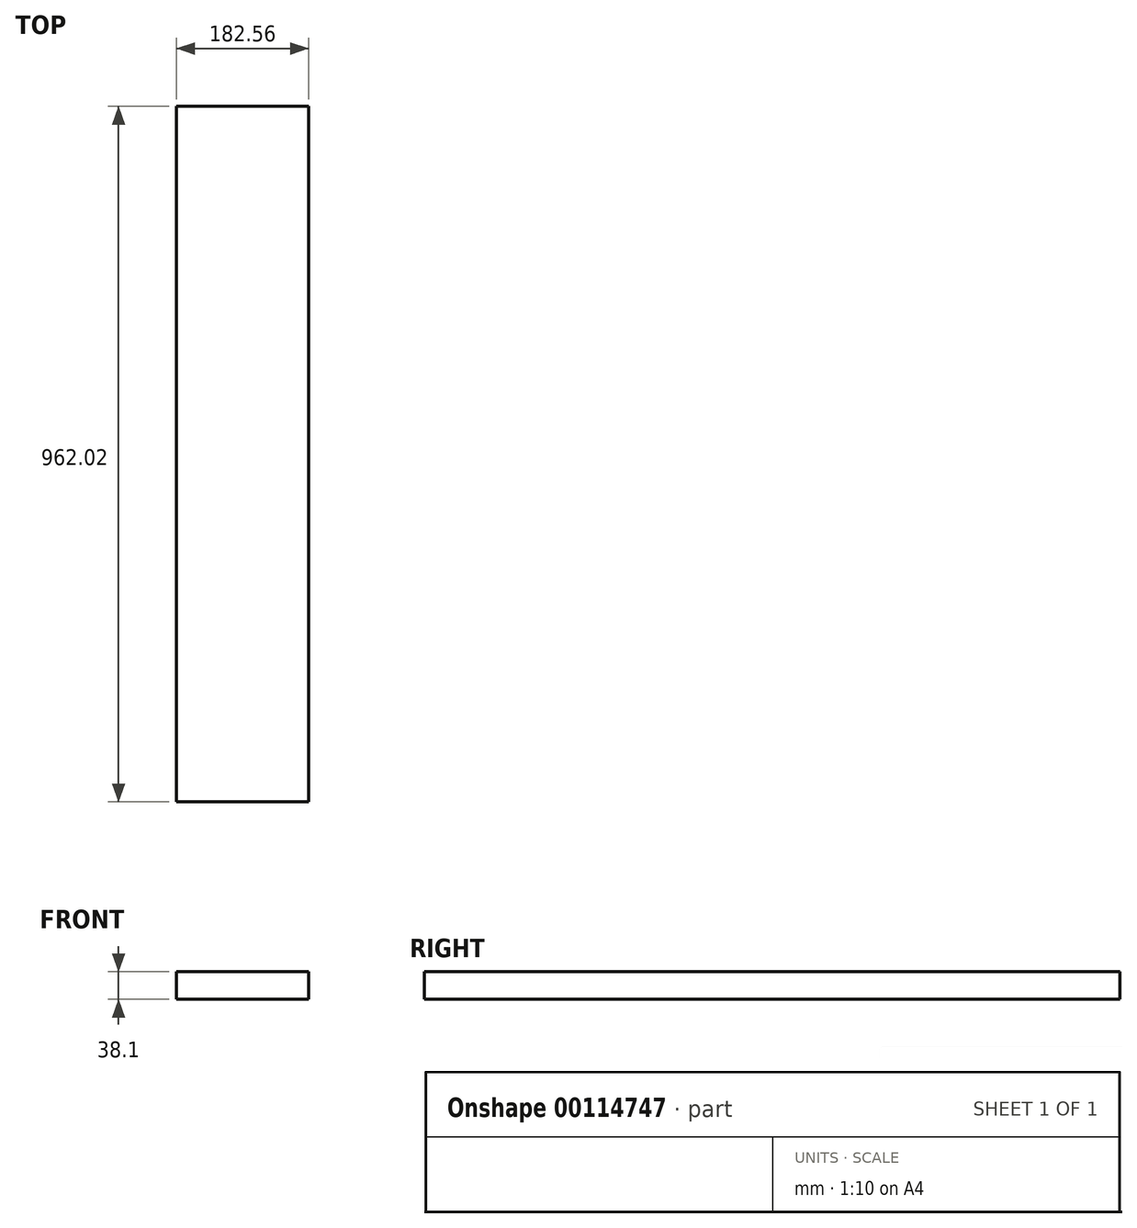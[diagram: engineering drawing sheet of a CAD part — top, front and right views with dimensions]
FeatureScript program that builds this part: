
annotation { "Feature Type Name" : "Feature", "Feature Type Description" : "" }
export const myFeature = defineFeature(function(context is Context, id is Id, definition is map)
    precondition{}
    {
        {
            var Q0;
            Q0=qCreatedBy(makeId("Top.planeOp"),FACE);
            var sketch = newSketch(context, id + "F0", { "sketchPlane" : qUnion([Q0])});
            skLineSegment(sketch, "E0.bottom", {"start": v(0, 0) * mm, "end": v(182.56, 0) * mm});
            skLineSegment(sketch, "E0.top", {"start": v(0, 962.03) * mm, "end": v(182.56, 962.03) * mm});
            skLineSegment(sketch, "E0.left", {"start": v(0, 0) * mm, "end": v(0, 962.02) * mm});
            skLineSegment(sketch, "E0.right", {"start": v(182.56, 0) * mm, "end": v(182.56, 962.03) * mm});
            skSolve(sketch);
        }
        {
            var Q0;
            Q0=qSketchRegion(id+"F0",true);
            extrude(context, id + "F1", {"entities" : qUnion([Q0]), "depth" : 38.1 * mm});
        }
    });
